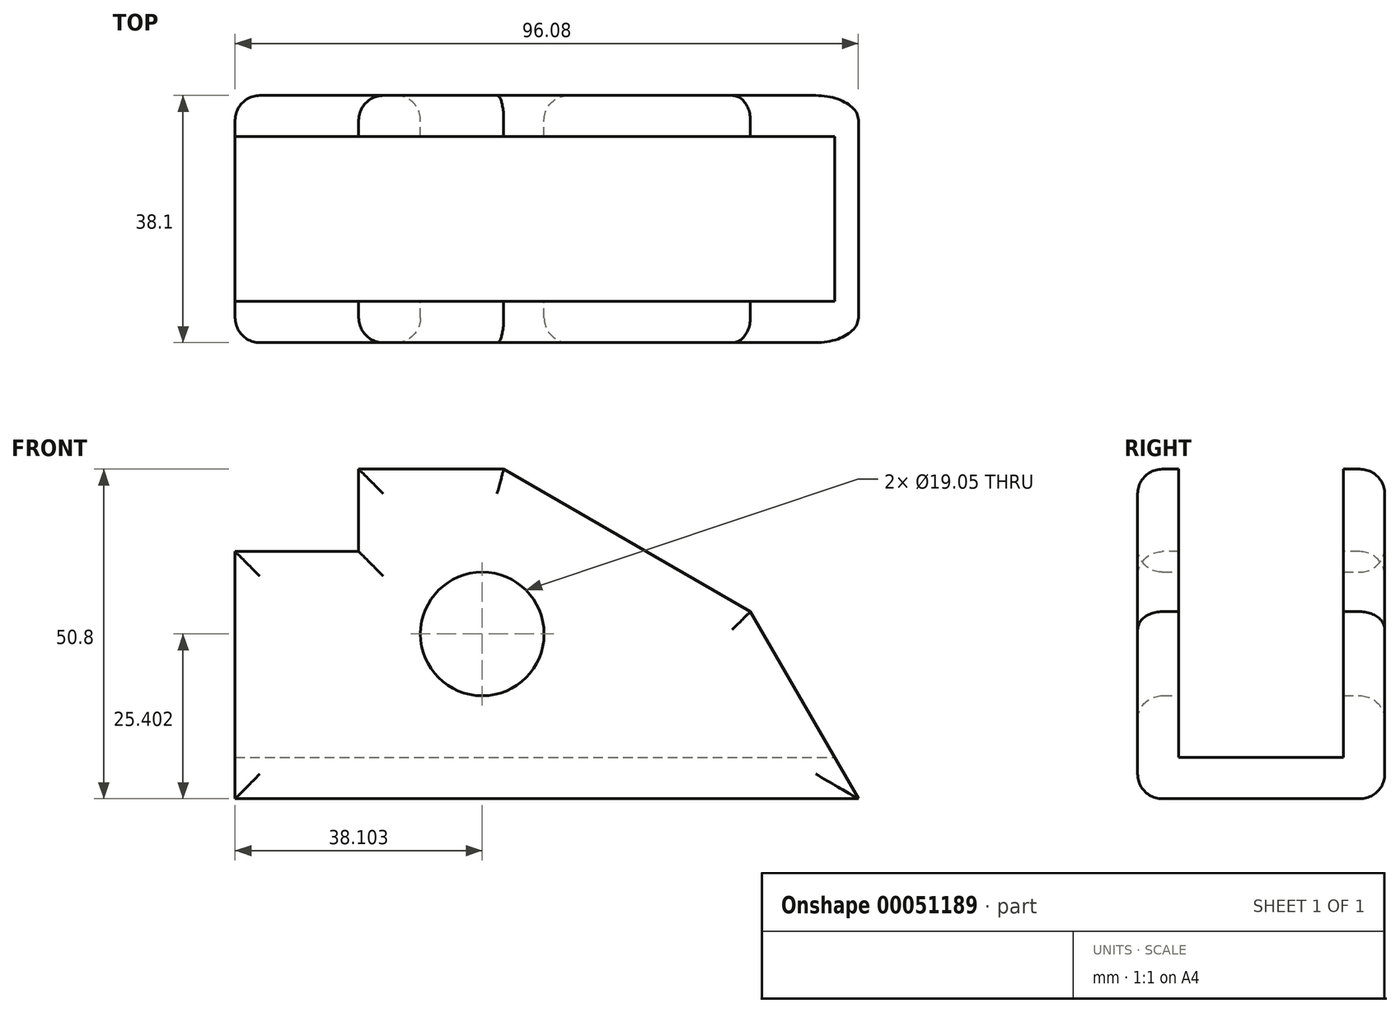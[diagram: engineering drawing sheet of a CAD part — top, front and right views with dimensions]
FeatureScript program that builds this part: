
annotation { "Feature Type Name" : "Feature", "Feature Type Description" : "" }
export const myFeature = defineFeature(function(context is Context, id is Id, definition is map)
    precondition{}
    {
        {
            var Q0;
            Q0=qCreatedBy(makeId("Front.planeOp"),FACE);
            var sketch = newSketch(context, id + "F0", { "sketchPlane" : qUnion([Q0])});
            skLineSegment(sketch, "E0", {"start": v(-52.18, 15.16) * mm, "end": v(-52.18, -35.64) * mm});
            skLineSegment(sketch, "E1", {"start": v(-52.18, 15.16) * mm, "end": v(-10.77, 15.16) * mm});
            skLineSegment(sketch, "E2", {"start": v(-10.77, 15.16) * mm, "end": v(27.25, -6.8) * mm});
            skLineSegment(sketch, "E3", {"start": v(-52.18, -35.64) * mm, "end": v(43.9, -35.64) * mm});
            skLineSegment(sketch, "E4", {"start": v(43.9, -35.64) * mm, "end": v(27.25, -6.8) * mm});
            skSolve(sketch);
        }
        {
            var Q0;
            Q0 = qSketchRegion(id + "F0", true);
            extrude(context, id + "F1", {"entities" : qUnion([Q0]), "depth" : 38.1 * mm});
        }
        {
            var Q0;
            Q0=qCreatedBy(makeId("Front.planeOp"),FACE);
            var sketch = newSketch(context, id + "F2", { "sketchPlane" : qUnion([Q0])});
            skCircle(sketch, "E5", {"center": v(-14.08, -10.24) * mm, "radius": 10.32 * mm});
            skSolve(sketch);
        }
        {
            var Q0;
            Q0=sQuery(id+"F2.wireOp",VERTEX,"E5.center");
            var Q1;
            Q1=makeQuery(id+"F1.opExtrude","SWEPT_BODY",BODY,{"disambiguationData":[OSD([sQuery(id+"F0.wireOp",EDGE,"E0"),sQuery(id+"F0.wireOp",EDGE,"E1"),sQuery(id+"F0.wireOp",EDGE,"E2"),sQuery(id+"F0.wireOp",EDGE,"E3"),sQuery(id+"F0.wireOp",EDGE,"E4")])]});
            hole(context, id + "F3", {"style" : HoleStyle.SIMPLE, "holeDiameter" : 19.05 * mm, "endStyle" : HoleEndStyle.THROUGH, "oppositeDirection" : true, "locations" : qUnion([Q0]), "scope" : qUnion([Q1])});
        }
        {
            var Q0;
            Q0=makeQuery(id+"F1.opExtrude","CAP_FACE",FACE,{"disambiguationData":[OSD([sQuery(id+"F0.wireOp",EDGE,"E0"),sQuery(id+"F0.wireOp",EDGE,"E1"),sQuery(id+"F0.wireOp",EDGE,"E2"),sQuery(id+"F0.wireOp",EDGE,"E3"),sQuery(id+"F0.wireOp",EDGE,"E4")])],"isStart":false});
            var sketch = newSketch(context, id + "F4", { "sketchPlane" : qUnion([Q0])});
            skLineSegment(sketch, "E6", {"start": v(-33.13, 15.16) * mm, "end": v(-33.13, 2.46) * mm});
            skLineSegment(sketch, "E7", {"start": v(-33.13, 2.46) * mm, "end": v(-52.18, 2.46) * mm});
            skSolve(sketch);
        }
        {
            var Q0;
            {var subQ0=sQuery(id+"F4.wireOp",EDGE,"E6");Q0=makeQuery(id+"F4.imprint","IMPRINT",FACE,{"disambiguationData":[TD([[makeQuery(id+"F4.imprint","IMPRINT",EDGE,{"derivedFrom":subQ0}),-1.0]])]});}
            extrude(context, id + "F5", {"entities" : qUnion([Q0]), "operationType" : NewBodyOperationType.REMOVE, "endBound" : BoundingType.THROUGH_ALL, "oppositeDirection" : true, "depth" : 25.4 * mm});
        }
        {
            var Q0;
            Q0=qCreatedBy(makeId("Right.planeOp"),FACE);
            var sketch = newSketch(context, id + "F6", { "sketchPlane" : qUnion([Q0])});
            skLineSegment(sketch, "E8.bottom", {"start": v(-6.35, 21.53) * mm, "end": v(-31.75, 21.53) * mm});
            skLineSegment(sketch, "E8.top", {"start": v(-6.35, -29.29) * mm, "end": v(-31.75, -29.29) * mm});
            skLineSegment(sketch, "E8.left", {"start": v(-6.35, 21.53) * mm, "end": v(-6.35, -29.29) * mm});
            skLineSegment(sketch, "E8.right", {"start": v(-31.75, 21.53) * mm, "end": v(-31.75, -29.29) * mm});
            skSolve(sketch);
        }
        {
            var Q0;
            Q0 = qSketchRegion(id + "F6", true);
            extrude(context, id + "F7", {"entities" : qUnion([Q0]), "operationType" : NewBodyOperationType.REMOVE, "endBound" : BoundingType.THROUGH_ALL, "oppositeDirection" : true, "depth" : 25.4 * mm});
        }
        {
            var Q0;
            Q0=makeQuery(id+"F7.boolean.opBoolean","COPY",FACE,{"derivedFrom":makeQuery(id+"F7.opExtrude","CAP_FACE",FACE,{"disambiguationData":[OSD([sQuery(id+"F6.wireOp",EDGE,"E8.bottom"),sQuery(id+"F6.wireOp",EDGE,"E8.top"),sQuery(id+"F6.wireOp",EDGE,"E8.left"),sQuery(id+"F6.wireOp",EDGE,"E8.right")])],"isStart":true})});
            extrude(context, id + "F8", {"entities" : qUnion([Q0]), "operationType" : NewBodyOperationType.REMOVE, "endBound" : BoundingType.THROUGH_ALL, "oppositeDirection" : true, "depth" : 25.4 * mm});
        }
        {
            var Q0;
            Q0=makeQuery(id+"F1.opExtrude","CAP_FACE",FACE,{"disambiguationData":[OSD([sQuery(id+"F0.wireOp",EDGE,"E0"),sQuery(id+"F0.wireOp",EDGE,"E1"),sQuery(id+"F0.wireOp",EDGE,"E2"),sQuery(id+"F0.wireOp",EDGE,"E3"),sQuery(id+"F0.wireOp",EDGE,"E4")])],"isStart":false});
            fillet(context, id + "F9", {"entities" : qUnion([Q0]), "radius" : 3.8 * mm, "tangentPropagation" : true, "allowEdgeOverflow" : false});
        }
        {
            var Q0;
            Q0=makeQuery(id+"F1.opExtrude","CAP_FACE",FACE,{"disambiguationData":[OSD([sQuery(id+"F0.wireOp",EDGE,"E0"),sQuery(id+"F0.wireOp",EDGE,"E1"),sQuery(id+"F0.wireOp",EDGE,"E2"),sQuery(id+"F0.wireOp",EDGE,"E3"),sQuery(id+"F0.wireOp",EDGE,"E4")])],"isStart":true});
            fillet(context, id + "F10", {"entities" : qUnion([Q0]), "radius" : 3.8 * mm, "tangentPropagation" : true, "allowEdgeOverflow" : false});
        }
    });
